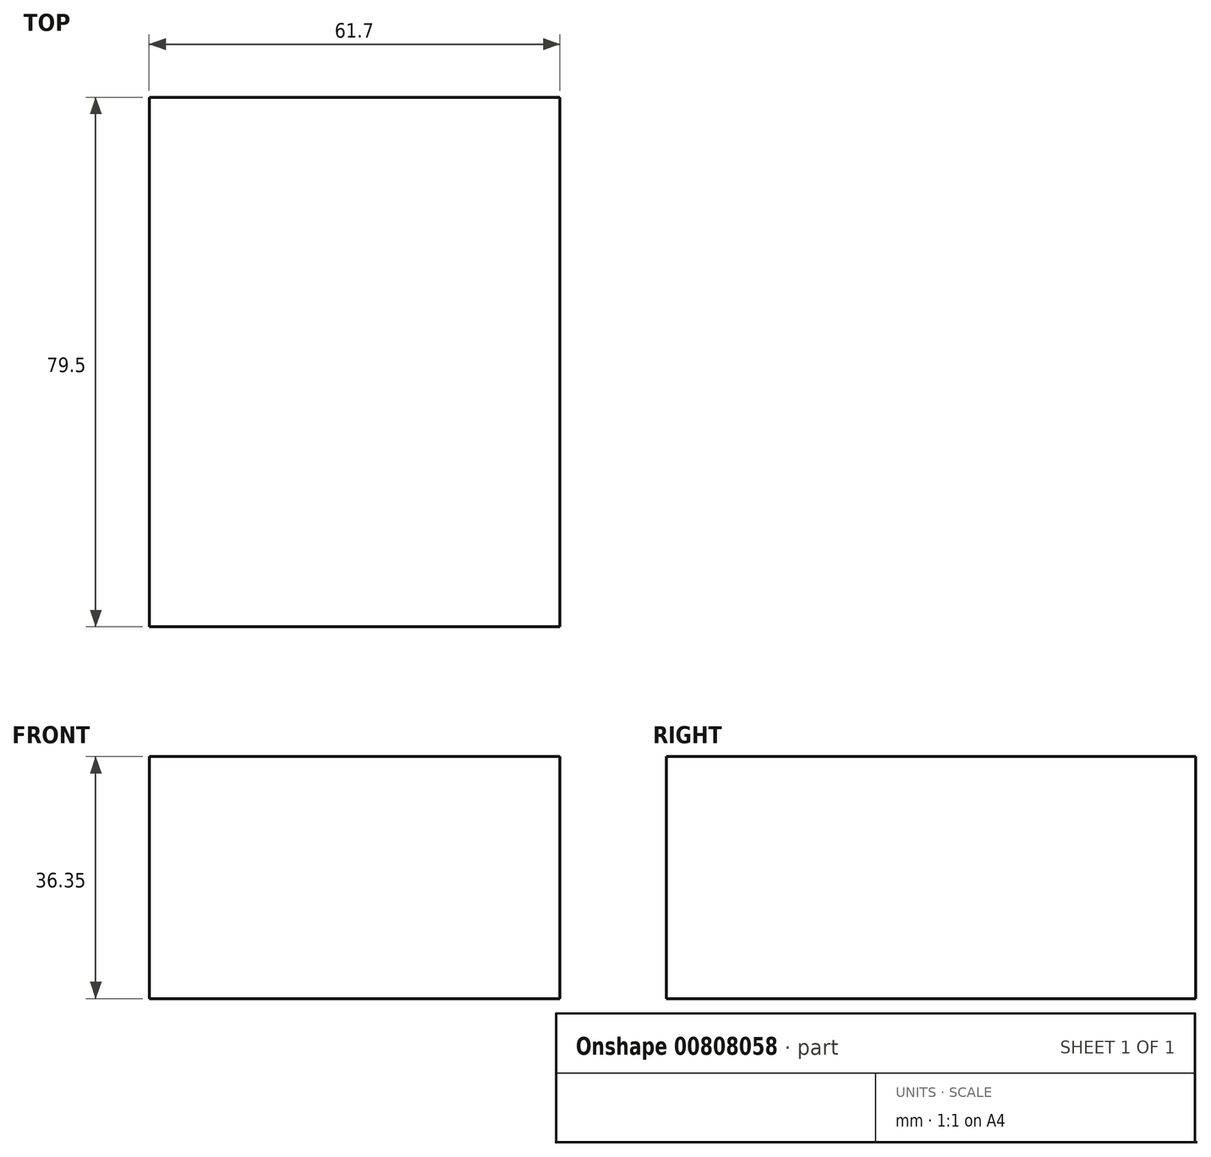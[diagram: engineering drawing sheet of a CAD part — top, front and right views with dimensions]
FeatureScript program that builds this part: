
annotation { "Feature Type Name" : "Feature", "Feature Type Description" : "" }
export const myFeature = defineFeature(function(context is Context, id is Id, definition is map)
    precondition{}
    {
        {
            var Q0;
            Q0=qCreatedBy(makeId("Front.planeOp"),FACE);
            var sketch = newSketch(context, id + "F0", { "sketchPlane" : qUnion([Q0])});
            skLineSegment(sketch, "E0.bottom", {"start": v(-144.02, 39.58) * mm, "end": v(-82.32, 39.58) * mm});
            skLineSegment(sketch, "E0.top", {"start": v(-144.02, 3.23) * mm, "end": v(-82.32, 3.23) * mm});
            skLineSegment(sketch, "E0.left", {"start": v(-144.02, 39.58) * mm, "end": v(-144.02, 3.23) * mm});
            skLineSegment(sketch, "E0.right", {"start": v(-82.32, 39.58) * mm, "end": v(-82.32, 3.23) * mm});
            skSolve(sketch);
        }
        {
            var Q0;
            Q0=makeQuery(id+"F0.imprint","IMPRINT",FACE,{"disambiguationData":[TD([[makeQuery(id+"F0.imprint","IMPRINT",EDGE,{"derivedFrom":sQuery(id+"F0.wireOp",EDGE,"E0.bottom")}),-1.0]])]});
            extrude(context, id + "F1", {"entities" : qUnion([Q0]), "depth" : 79.5 * mm, "offsetDistance" : 25.4 * mm});
        }
    });
